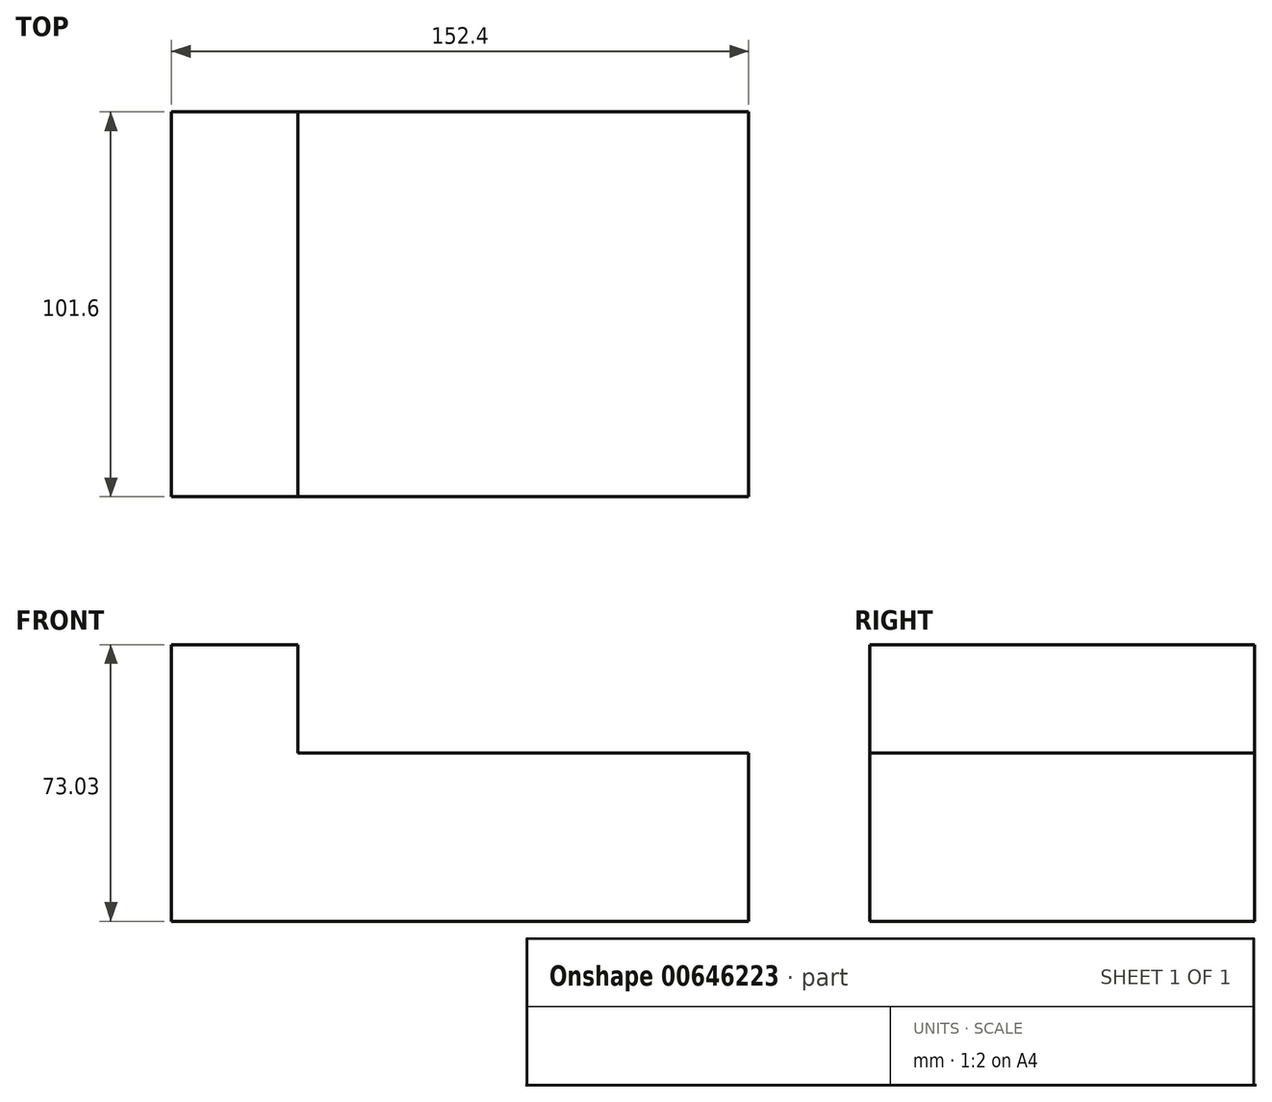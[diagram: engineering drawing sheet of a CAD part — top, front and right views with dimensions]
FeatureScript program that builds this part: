
annotation { "Feature Type Name" : "Feature", "Feature Type Description" : "" }
export const myFeature = defineFeature(function(context is Context, id is Id, definition is map)
    precondition{}
    {
        {
            var Q0;
            Q0=qCreatedBy(makeId("Front.planeOp"),FACE);
            var sketch = newSketch(context, id + "F0", { "sketchPlane" : qUnion([Q0])});
            skLineSegment(sketch, "E0", {"start": v(-160.25, -6.85) * mm, "end": v(-160.25, -79.88) * mm});
            skLineSegment(sketch, "E1", {"start": v(-7.85, -79.88) * mm, "end": v(-160.25, -79.88) * mm});
            skLineSegment(sketch, "E2", {"start": v(-7.85, -35.43) * mm, "end": v(-7.85, -79.88) * mm});
            skLineSegment(sketch, "E3", {"start": v(-7.85, -35.43) * mm, "end": v(-126.91, -35.43) * mm});
            skLineSegment(sketch, "E4", {"start": v(-160.25, -6.85) * mm, "end": v(-126.91, -6.85) * mm});
            skLineSegment(sketch, "E5", {"start": v(-126.91, -35.43) * mm, "end": v(-126.91, -6.85) * mm});
            skSolve(sketch);
        }
        {
            var Q0;
            Q0=makeQuery(id+"F0.imprint","IMPRINT",FACE,{"disambiguationData":[TD([[makeQuery(id+"F0.imprint","IMPRINT",EDGE,{"derivedFrom":sQuery(id+"F0.wireOp",EDGE,"E0")}),1.0]])]});
            extrude(context, id + "F1", {"entities" : qUnion([Q0]), "depth" : 25.4 * mm, "offsetDistance" : 25.4 * mm});
        }
        {
            var Q0;
            Q0=makeQuery(id+"F1.opExtrude","CAP_FACE",FACE,{"disambiguationData":[OSD([sQuery(id+"F0.wireOp",EDGE,"E0"),sQuery(id+"F0.wireOp",EDGE,"E1"),sQuery(id+"F0.wireOp",EDGE,"E2"),sQuery(id+"F0.wireOp",EDGE,"E3"),sQuery(id+"F0.wireOp",EDGE,"E4"),sQuery(id+"F0.wireOp",EDGE,"E5")])],"isStart":false});
            extrude(context, id + "F2", {"entities" : qUnion([Q0]), "operationType" : NewBodyOperationType.ADD, "depth" : 25.4 * mm, "offsetDistance" : 25.4 * mm});
        }
        {
            var Q0;
            Q0=makeQuery(id+"F2.opExtrude","CAP_FACE",FACE,{"disambiguationData":[OSD([sQuery(id+"F0.wireOp",EDGE,"E0"),sQuery(id+"F0.wireOp",EDGE,"E1"),sQuery(id+"F0.wireOp",EDGE,"E2"),sQuery(id+"F0.wireOp",EDGE,"E3"),sQuery(id+"F0.wireOp",EDGE,"E4"),sQuery(id+"F0.wireOp",EDGE,"E5")])],"isStart":false});
            extrude(context, id + "F3", {"entities" : qUnion([Q0]), "operationType" : NewBodyOperationType.ADD, "depth" : 50.8 * mm, "offsetDistance" : 25.4 * mm});
        }
    });
